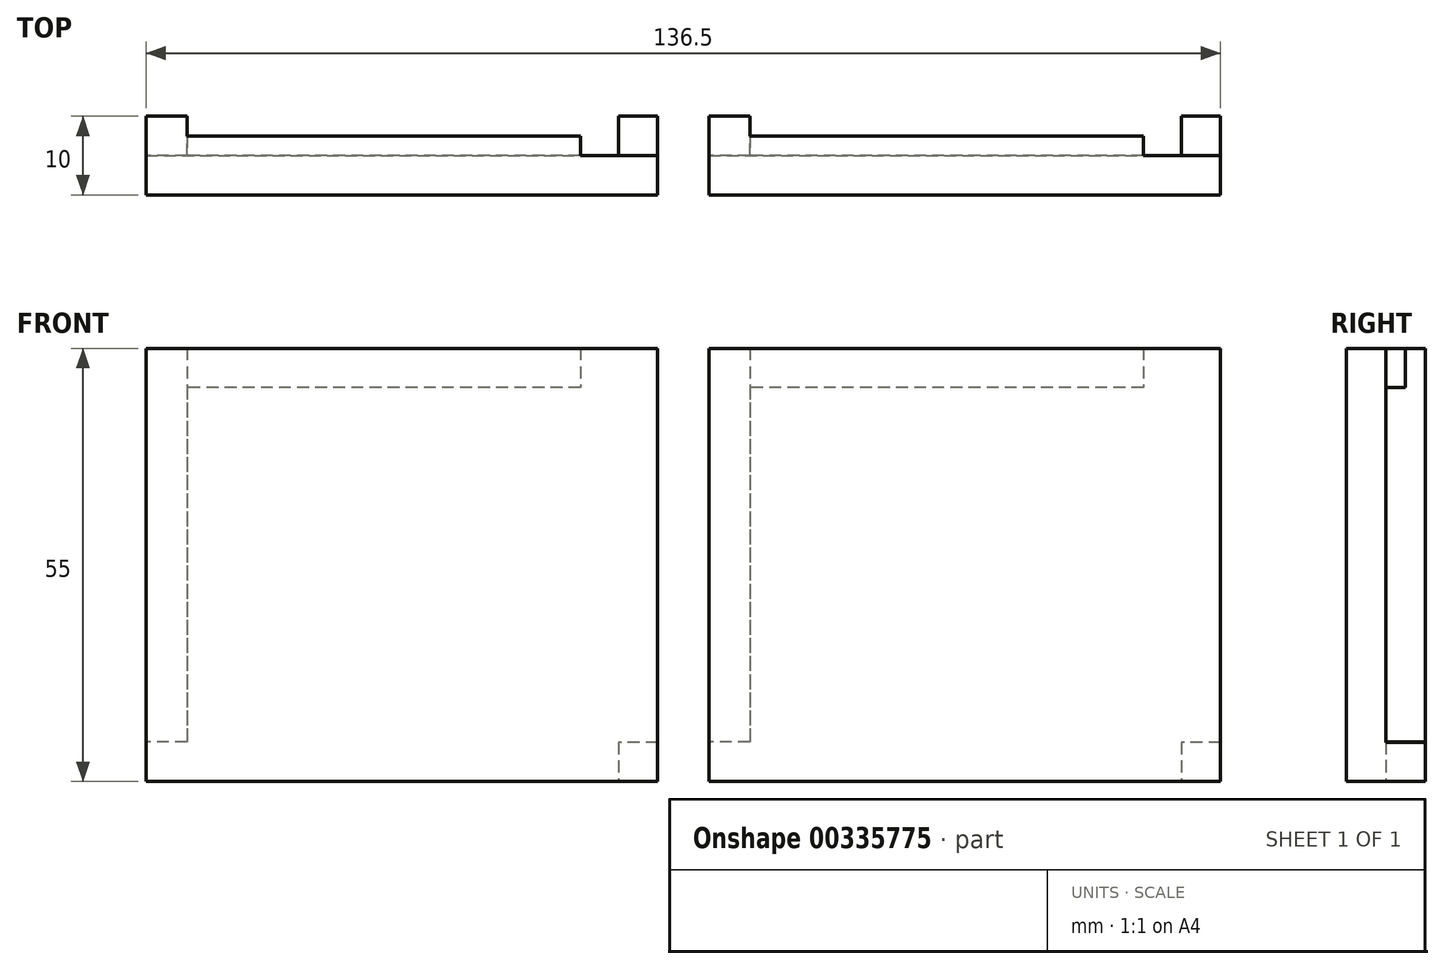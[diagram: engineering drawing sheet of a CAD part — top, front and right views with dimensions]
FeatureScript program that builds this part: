
annotation { "Feature Type Name" : "Feature", "Feature Type Description" : "" }
export const myFeature = defineFeature(function(context is Context, id is Id, definition is map)
    precondition{}
    {
        {
            var Q0;
            Q0=qCreatedBy(makeId("Front.planeOp"),FACE);
            var sketch = newSketch(context, id + "F0", { "sketchPlane" : qUnion([Q0])});
            skLineSegment(sketch, "E0.bottom", {"start": v(0, 0) * mm, "end": v(65, 0) * mm});
            skLineSegment(sketch, "E0.top", {"start": v(0, -55) * mm, "end": v(65, -55) * mm});
            skLineSegment(sketch, "E0.left", {"start": v(0, 0) * mm, "end": v(0, -55) * mm});
            skLineSegment(sketch, "E0.right", {"start": v(65, 0) * mm, "end": v(65, -55) * mm});
            skSolve(sketch);
        }
        {
            var Q0;
            Q0=qCreatedBy(makeId("Right.planeOp"),FACE);
            var sketch = newSketch(context, id + "F1", { "sketchPlane" : qUnion([Q0])});
            skLineSegment(sketch, "E1.bottom", {"start": v(0, 0) * mm, "end": v(5, 0) * mm});
            skLineSegment(sketch, "E1.top", {"start": v(0, -50) * mm, "end": v(5, -50) * mm});
            skLineSegment(sketch, "E1.left", {"start": v(0, 0) * mm, "end": v(0, -50) * mm});
            skLineSegment(sketch, "E1.right", {"start": v(5, 0) * mm, "end": v(5, -50) * mm});
            skSolve(sketch);
        }
        {
            var Q0;
            Q0=qCreatedBy(makeId("Front.planeOp"),FACE);
            var sketch = newSketch(context, id + "F2", { "sketchPlane" : qUnion([Q0])});
            skLineSegment(sketch, "E2.bottom", {"start": v(55.2, 0) * mm, "end": v(5.2, 0) * mm});
            skLineSegment(sketch, "E2.top", {"start": v(55.2, -5) * mm, "end": v(5.2, -5) * mm});
            skLineSegment(sketch, "E2.left", {"start": v(55.2, 0) * mm, "end": v(55.2, -5) * mm});
            skLineSegment(sketch, "E2.right", {"start": v(5.2, 0) * mm, "end": v(5.2, -5) * mm});
            skSolve(sketch);
        }
        {
            var Q0;
            Q0=makeQuery(id+"F0.imprint","IMPRINT",FACE,{"disambiguationData":[TD([[makeQuery(id+"F0.imprint","IMPRINT",EDGE,{"derivedFrom":sQuery(id+"F0.wireOp",EDGE,"E0.bottom")}),-1.0]])]});
            extrude(context, id + "F3", {"entities" : qUnion([Q0]), "depth" : 5 * mm});
        }
        {
            var Q0;
            Q0=makeQuery(id+"F2.imprint","IMPRINT",FACE,{"disambiguationData":[TD([[makeQuery(id+"F2.imprint","IMPRINT",EDGE,{"derivedFrom":sQuery(id+"F2.wireOp",EDGE,"E2.bottom")}),1.0]])]});
            extrude(context, id + "F4", {"entities" : qUnion([Q0]), "operationType" : NewBodyOperationType.ADD, "oppositeDirection" : true, "depth" : 2.5 * mm});
        }
        {
            var Q0;
            Q0=makeQuery(id+"F1.imprint","IMPRINT",FACE,{"disambiguationData":[TD([[makeQuery(id+"F1.imprint","IMPRINT",EDGE,{"derivedFrom":sQuery(id+"F1.wireOp",EDGE,"E1.bottom")}),-1.0]])]});
            extrude(context, id + "F5", {"entities" : qUnion([Q0]), "operationType" : NewBodyOperationType.ADD, "depth" : 5.2 * mm});
        }
        {
            var Q0;
            Q0=qCreatedBy(makeId("Front.planeOp"),FACE);
            var sketch = newSketch(context, id + "F6", { "sketchPlane" : qUnion([Q0])});
            skLineSegment(sketch, "E3.bottom", {"start": v(65, -50.05) * mm, "end": v(60, -50.05) * mm});
            skLineSegment(sketch, "E3.top", {"start": v(65, -55) * mm, "end": v(60, -55) * mm});
            skLineSegment(sketch, "E3.left", {"start": v(65, -50.05) * mm, "end": v(65, -55) * mm});
            skLineSegment(sketch, "E3.right", {"start": v(60, -50.05) * mm, "end": v(60, -55) * mm});
            skSolve(sketch);
        }
        {
            var Q0;
            Q0=makeQuery(id+"F6.imprint","IMPRINT",FACE,{"disambiguationData":[TD([[makeQuery(id+"F6.imprint","IMPRINT",EDGE,{"derivedFrom":sQuery(id+"F6.wireOp",EDGE,"E3.bottom")}),1.0]])]});
            extrude(context, id + "F7", {"entities" : qUnion([Q0]), "operationType" : NewBodyOperationType.ADD, "oppositeDirection" : true, "depth" : 5 * mm});
        }
        {
            var Q0;
            Q0=makeQuery(id+"F3.opExtrude","SWEPT_BODY",BODY,{"disambiguationData":[OSD([sQuery(id+"F0.wireOp",EDGE,"E0.bottom"),sQuery(id+"F0.wireOp",EDGE,"E0.top"),sQuery(id+"F0.wireOp",EDGE,"E0.left"),sQuery(id+"F0.wireOp",EDGE,"E0.right")])]});
            transform(context, id + "F8", {"entities" : qUnion([Q0]), "transformType" : TransformType.TRANSLATION_3D, "dx" : -71.5 * mm, "dy" : 0 * mm, "dz" : 0 * mm, "makeCopy" : true});
        }
        {
            var Q0;
            Q0=makeQuery(id+"F3.opExtrude","SWEPT_BODY",BODY,{"disambiguationData":[OSD([sQuery(id+"F0.wireOp",EDGE,"E0.bottom"),sQuery(id+"F0.wireOp",EDGE,"E0.top"),sQuery(id+"F0.wireOp",EDGE,"E0.left"),sQuery(id+"F0.wireOp",EDGE,"E0.right")])]});
            transform(context, id + "F9", {"entities" : qUnion([Q0]), "transformType" : TransformType.TRANSLATION_3D, "dx" : 0 * mm, "dy" : 0 * mm, "dz" : 0 * mm, "makeCopy" : true});
        }
    });
